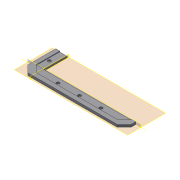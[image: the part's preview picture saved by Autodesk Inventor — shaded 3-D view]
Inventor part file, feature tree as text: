
AUTODESK INVENTOR PART (.ipt)
format: ipt  version: 2015 SP2 (Build 190223200, 223)  size: 124,416 bytes
history: native  units: mm
features: extrude x4, sketch x3, reference x2, other x1, pattern_linear x1
ambient origin geometry x8: Origin, YZ Plane, XZ Plane, XY Plane, X Axis, Y Axis, Z Axis, Center Point
bodies: Body1 (feature_tree)
feature tree (11):
  other  "Sólido1"
  extrude  "Extrusión1"  Depth=107.005mm
  extrude  "Extrusión2"  Depth=27.0mm
  extrude  "Extrusión3"  Depth=1.0mm
  pattern_linear  "Patrón rectangular1"  Spacing1=15.0mm  [1 undecoded]
  extrude  "Extrusión4"  Depth=1.0mm
  sketch  "Boceto2"  dims[d0=107.005mm d1=5.5mm]
  sketch  "Boceto3"  dims[d5=32.5mm d8=27.0mm]
  sketch  "Boceto4"  dims[d9=3.0mm d10=0.0mm d11=3.78mm d12=15.0mm d13=5.5mm d14=3.0mm d15=0.0mm d16=3.78mm d17=5.5mm d18=35.0mm d19=3.0mm d20=0.0mm d21=30.0mm d23=25.0mm d24=8.5mm d25=8.5mm d26=135.0deg d27=11.314mm d28=1.0mm d30=12.5mm d31=4.5mm d32=1.0mm d33=0.0mm d34=135.0deg]
  reference  "Referencia1"
  reference  "Referencia2"
note: 1 required parameter value undecoded (feature->parameter linkage not recoverable at this tier; creation-order binding heuristic only, values carry confidence <= 0.55)
